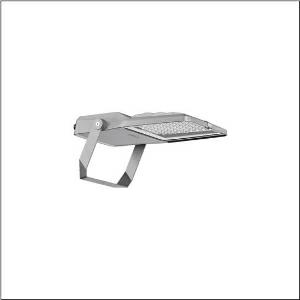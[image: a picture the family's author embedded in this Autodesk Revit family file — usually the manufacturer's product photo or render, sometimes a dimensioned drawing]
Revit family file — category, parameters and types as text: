
# Revit family: floodlight_fl_21_iq_mini___pl33t_5xa7772c1f1a_9de6
name_source: partatom
category: Lighting Fixtures
units: mm (PartAtom-declared; Revit-internal decimal feet)

## family parameters
Cut with Voids When Loaded = No
Host = Face
Light Source = No
Part Type = Normal
Room Calculation Point = No
Round Connector Dimension = Use Diameter
Shared = No

## types (1)
- --- (1 x LED, 10000 lm, 87.2 W, 2200K)
    Apparent Load = 87 VA
    CIE Flux Codes = 26 75 99 100 100
    Color Rendering = 70
    Color Temperature = 2200K
    Default Elevation = 1800 mm
    Description = Floodlight FL 21 iQ mini, floodlight, primary light control with lens, of PMMA, primary optical cover: protective disc, of toughened safety glass, transparent, light distribution: PL33T, light emission: direct distribution, installation type: surface-mounted, LED, High Power LED, rated luminous flux: 10.000lm, luminous efficacy: 115lm/W, light colour: 722, colour temperature: 2200K, control gear: iQ Street-Remote/DALI, control: Street-Remote, Auto-Match, Temp-Guard, Night-Set, Smart-Wire, Desk-Remote (wireless, voltage-free reading and setting of iQ features in the workshop via application-optimized NFC function/RFID function), optimised constant luminous flux control (CLO 2.0), with terminal, 6-pole, mains connection: 220..240V, AC, 50/60Hz, start of lifetime: 87W, end of service life: 92W, reduction: 40W, luminaire housing, of diecast aluminium, powder-coated, Siteco® metallic grey (DB 702S), corrosivity category C5 mid according to DIN EN ISO 12944, suitable for swimming pools, chlorine-resistant, sealing non-destructively replaceable, mounting bracket, of steel, galvanised, powder-coated, Siteco® metallic grey (DB 702S), protection rating (complete): IP66, insulation class (complete): insulation class II (safety insulation), certification: CE, ENEC, VDE, protection symbol: D, impact resistance: IK08, permissible operating ambient temperature: -40..+40°C, permissible operating ambient temperature for outdoor applications: -40..+50°C, standard: DIN EN 12944, LABS conformity tested according to VDMA 24364:2018-05, packaging unit: 1 piece

Light Distribution: PL33T
    Height = 70 mm
    Lamp = 1 x LED
    Lamp Light Flux = 10000 lm
    Lamp Power = 87.2 W
    Lamp count = 1
    Length = 485 mm
    Luminous efficacy = 115 lm/W
    Manufacturer = Siteco
    ModVariant = No
    Model = 5XA7772C1F1A
    Number of Poles = 1
    OnlyDefault = Yes
    Power Factor = 1
    Product Name = Floodlight FL 21 iQ mini | PL33T
    Product group = floodlight | pylon annexe
    ProductGroupID = 6200
    Protection Class = Protection class II
    Protection Degree = IP 66
    RLX_Detail_Level = 1
    RLX_Emergency_Light_Flux = 0 lm
    RLX_Emergency_Type = 0
    RLX_Emergency_Type_DB = No
    RlxData = <blob elided: 96101 chars, md5=81c5c4b4>
    Socket = socket
    Standby Power = 0 W
    System Light Flux = 10000 lm
    System Power = 87 W
    Type Comments = factory setting: luminous flux: 100 % | dim-lin: 254 | 456 mA
    Type Image = l_1006845.jpg
    URL = http://relux.com
    VarID = @adj_149600
    Voltage = 0 V
    Weight = 0.00 kg
    Width = 337 mm

## geometry (parser evidence)
native form markers: Blend x4, Sweep x13
no freeform markers — native parametric forms only
